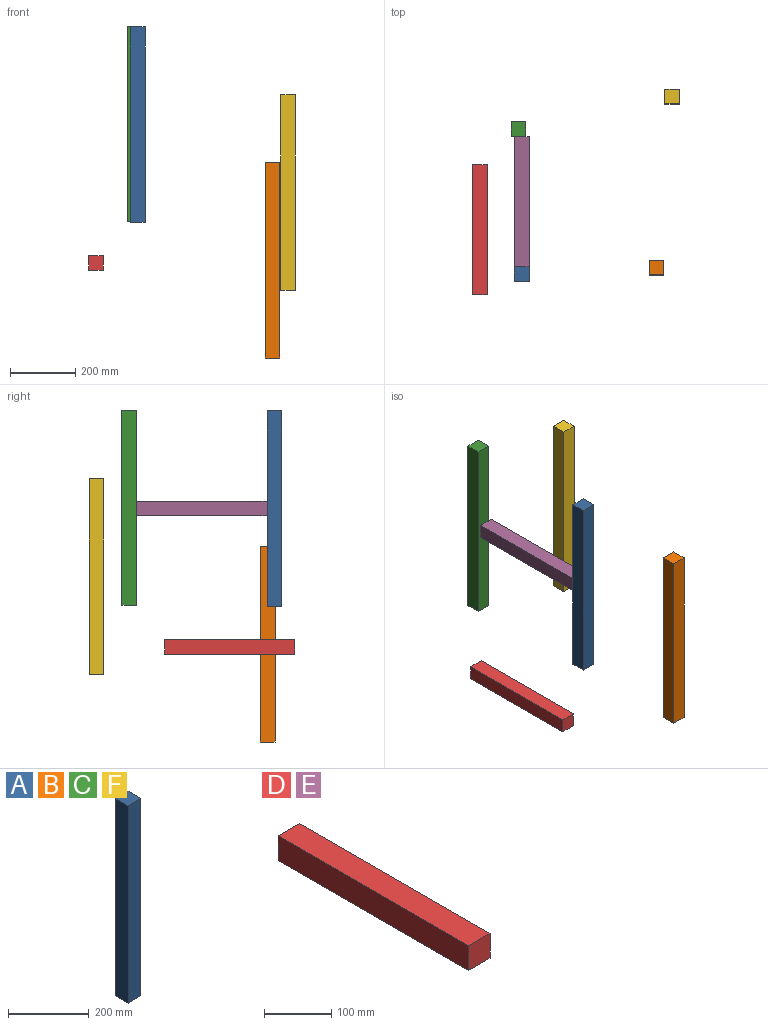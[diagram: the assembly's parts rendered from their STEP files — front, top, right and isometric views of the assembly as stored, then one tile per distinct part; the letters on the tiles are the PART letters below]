
ASSEMBLY  parts=6 mates=2
PART A: 6 faces, bbox 45x45x600 mm
  f0: plane 600x45mm, normal (0,1,0), area 27000mm2, adj f1,f3,f4,f5
  f1: plane 600x45mm, normal (-1,0,0), area 27000mm2, adj f0,f2,f4,f5
  f2: plane 600x45mm, normal (0,-1,0), area 27000mm2, adj f1,f3,f4,f5
  f3: plane 600x45mm, normal (1,0,0), area 27000mm2, adj f0,f2,f4,f5
  f4: plane 45x45mm, normal (0,0,1), area 2025mm2, adj f0,f1,f2,f3
  f5: plane 45x45mm, normal (0,0,-1), area 2025mm2, adj f0,f1,f2,f3
PART B: same geometry as A
PART C: same geometry as A
PART D: 6 faces, bbox 45x400x45 mm
  f0: plane 400x45mm, normal (0,0,1), area 18000mm2, adj f1,f3,f4,f5
  f1: plane 400x45mm, normal (-1,0,0), area 18000mm2, adj f0,f2,f4,f5
  f2: plane 400x45mm, normal (0,0,-1), area 18000mm2, adj f1,f3,f4,f5
  f3: plane 400x45mm, normal (1,0,0), area 18000mm2, adj f0,f2,f4,f5
  f4: plane 45x45mm, normal (0,-1,0), area 2025mm2, adj f0,f1,f2,f3
  f5: plane 45x45mm, normal (0,1,0), area 2025mm2, adj f0,f1,f2,f3
PART E: same geometry as D
PART F: same geometry as A
PLACE A at identity
PLACE B t=(413.52,20.36,-416.92)mm
PLACE C t=(-10.28,445.66,2.97)mm
PLACE D t=(-223.9,314.59,-102.26)mm
PLACE E t=(-95.17,400,322.5)mm
PLACE F t=(461.89,546.26,-208.69)mm
MATE parallel E.f4 <-> A.f0  axis (0,-1,0) through (-72.67,0,300)mm
MATE parallel E.f5 <-> C.f2  axis (0,1,0) through (-72.67,400,300)mm
